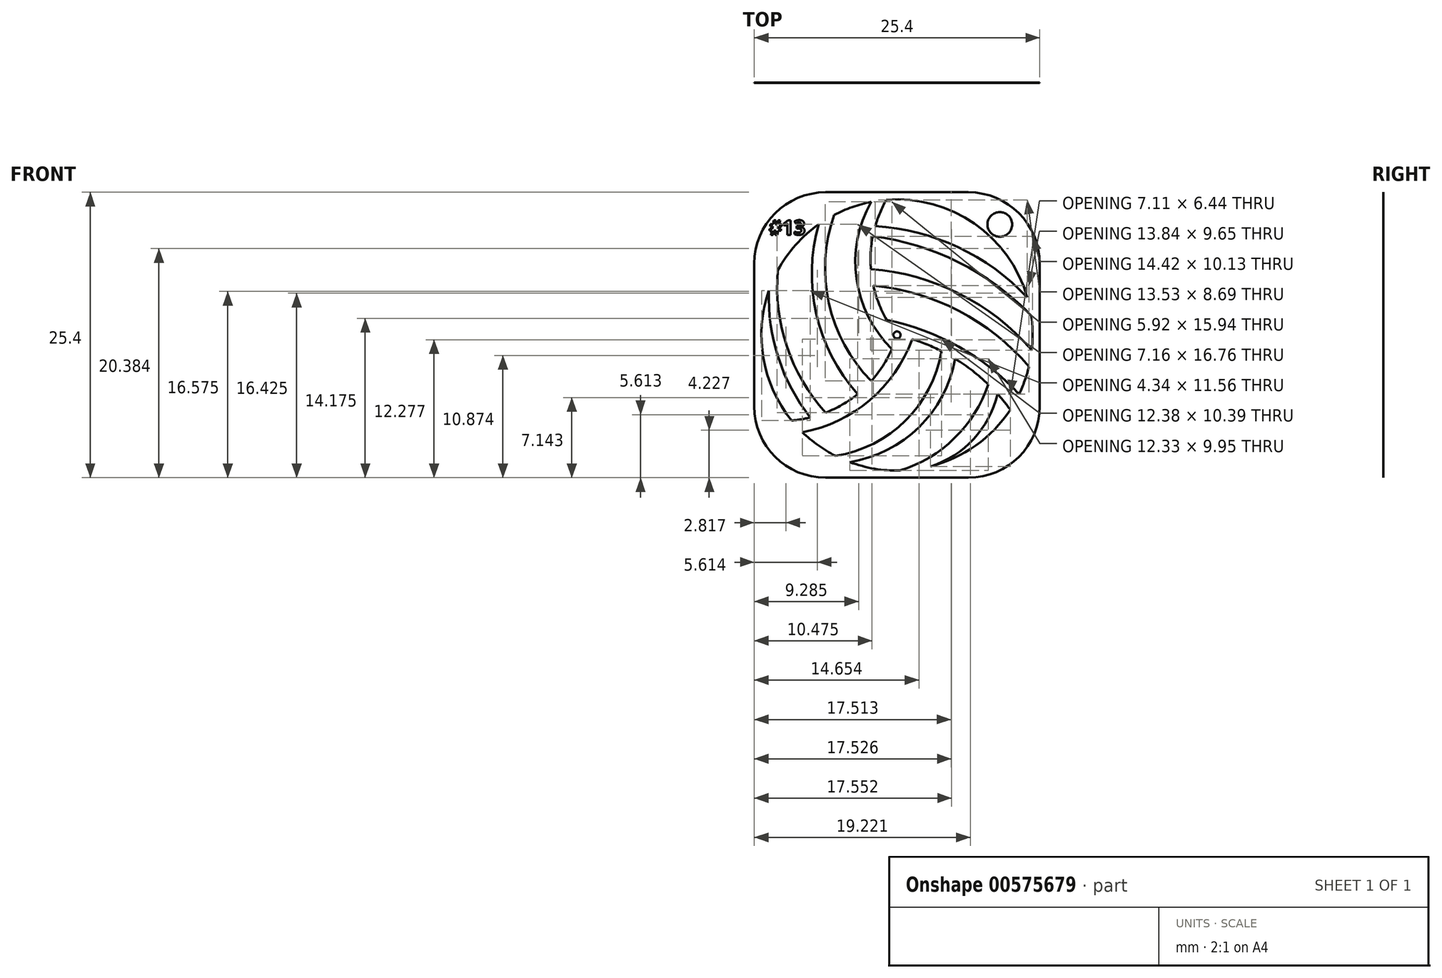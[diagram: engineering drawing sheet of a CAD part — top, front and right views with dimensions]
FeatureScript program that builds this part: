
annotation { "Feature Type Name" : "Feature", "Feature Type Description" : "" }
export const myFeature = defineFeature(function(context is Context, id is Id, definition is map)
    precondition{}
    {
        {
            var Q0;
            Q0=qCreatedBy(makeId("Front.planeOp"),FACE);
            var sketch = newSketch(context, id + "F0", { "sketchPlane" : qUnion([Q0])});
            skLineSegment(sketch, "E0", {"start": v(0, 6.35) * mm, "end": v(0, 19.05) * mm});
            skLineSegment(sketch, "E1", {"start": v(6.35, 0) * mm, "end": v(19.05, 0) * mm});
            skLineSegment(sketch, "E2", {"start": v(25.4, 6.35) * mm, "end": v(25.4, 19.05) * mm});
            skLineSegment(sketch, "E3", {"start": v(19.05, 25.4) * mm, "end": v(6.35, 25.4) * mm});
            skCircle(sketch, "E4", {"center": v(12.7, 12.7) * mm, "radius": 12.07 * mm});
            skPoint(sketch, "E5.visualSharp", {"position": v(0, 25.4) * mm});
            skArc(sketch, "E5.filletArc", {"start": v(6.35, 25.4) * mm, "mid": v(1.86, 23.54) * mm, "end": v(0, 19.05) * mm});
            skPoint(sketch, "E6.visualSharp", {"position": v(0, 0) * mm});
            skArc(sketch, "E6.filletArc", {"start": v(0, 6.35) * mm, "mid": v(1.86, 1.86) * mm, "end": v(6.35, 0) * mm});
            skPoint(sketch, "E7.visualSharp", {"position": v(25.4, 0) * mm});
            skArc(sketch, "E7.filletArc", {"start": v(19.05, 0) * mm, "mid": v(23.54, 1.86) * mm, "end": v(25.4, 6.35) * mm});
            skPoint(sketch, "E8.visualSharp", {"position": v(25.4, 25.4) * mm});
            skArc(sketch, "E8.filletArc", {"start": v(25.4, 19.05) * mm, "mid": v(23.54, 23.54) * mm, "end": v(19.05, 25.4) * mm});
            skPoint(sketch, "E9.centerSnap0", {"position": v(23.54, 23.54) * mm});
            skCircle(sketch, "E10", {"center": v(21.84, 22.54) * mm, "radius": 1.1 * mm});
            skPoint(sketch, "E9.center.orphan", {"position": v(21.97, 23.54) * mm});
            skArc(sketch, "E11", {"start": v(11.75, 24.73) * mm, "mid": v(10.37, 18.57) * mm, "end": v(12.7, 12.7) * mm});
            skArc(sketch, "E12", {"start": v(22.78, 6.06) * mm, "mid": v(18.34, 10.3) * mm, "end": v(12.7, 12.7) * mm});
            skArc(sketch, "E13", {"start": v(3.33, 5.1) * mm, "mid": v(9.2, 7.45) * mm, "end": v(12.7, 12.7) * mm});
            skLineSegment(sketch, "E14", {"start": v(15.68, 24.4) * mm, "end": v(15.68, 24.4) * mm});
            skPoint(sketch, "E15.start.orphan", {"position": v(19.05, 22.96) * mm});
            skArc(sketch, "E16", {"start": v(7.22, 1.95) * mm, "mid": v(13.45, 5.08) * mm, "end": v(16.67, 11.26) * mm});
            skArc(sketch, "E17", {"start": v(12.96, 0.64) * mm, "mid": v(17.81, 3.52) * mm, "end": v(20.82, 8.3) * mm});
            skArc(sketch, "E18", {"start": v(24.43, 9.9) * mm, "mid": v(18.2, 14.84) * mm, "end": v(10.6, 17.1) * mm});
            skArc(sketch, "E19", {"start": v(24.64, 14.44) * mm, "mid": v(18.2, 19.17) * mm, "end": v(10.54, 21.5) * mm});
            skArc(sketch, "E20", {"start": v(7.1, 23.4) * mm, "mid": v(6.64, 15.53) * mm, "end": v(10.4, 8.6) * mm});
            skArc(sketch, "E21", {"start": v(2.1, 18.46) * mm, "mid": v(2.9, 11.68) * mm, "end": v(6.35, 5.8) * mm});
            skArc(sketch, "E22", {"start": v(10.4, 24.54) * mm, "mid": v(9.1, 17.69) * mm, "end": v(12.25, 11.46) * mm});
            skArc(sketch, "E23", {"start": v(5.74, 22.56) * mm, "mid": v(5.52, 14.56) * mm, "end": v(9.2, 7.45) * mm});
            skArc(sketch, "E24", {"start": v(1.3, 16.65) * mm, "mid": v(2.14, 10.68) * mm, "end": v(4.99, 5.36) * mm});
            skArc(sketch, "E25", {"start": v(23.56, 7.45) * mm, "mid": v(18.19, 11.67) * mm, "end": v(11.78, 14.04) * mm});
            skArc(sketch, "E26", {"start": v(24.7, 11.36) * mm, "mid": v(18.24, 16.38) * mm, "end": v(10.37, 18.57) * mm});
            skArc(sketch, "E27", {"start": v(4.28, 4.05) * mm, "mid": v(10.27, 6.9) * mm, "end": v(14.04, 12.34) * mm});
            skArc(sketch, "E28", {"start": v(8.49, 1.4) * mm, "mid": v(14.65, 4.5) * mm, "end": v(17.87, 10.59) * mm});
            skArc(sketch, "E29", {"start": v(15.67, 1) * mm, "mid": v(19.5, 3.44) * mm, "end": v(21.65, 7.45) * mm});
            skPoint(sketch, "E30.start.orphan", {"position": v(24.3, 16.04) * mm});
            skArc(sketch, "E31", {"start": v(24.3, 16.04) * mm, "mid": v(18.13, 20.5) * mm, "end": v(10.76, 22.38) * mm});
            skCircle(sketch, "E32", {"center": v(12.7, 12.7) * mm, "radius": 0.32 * mm});
            skText(sketch, "E33", { "text": "#13", "fontName": "OpenSans-Bold.ttf"});
            skLineSegment(sketch, "E34", {"start": v(0.36, 21.14) * mm, "end": v(0.36, 5.6) * mm});
            skLineSegment(sketch, "E35", {"start": v(0.36, 17.45) * mm, "end": v(0, 17.45) * mm});
            const initialGuessF0  = {"E33": [0.00131, 0.02162, 1, 0, 0.0013], "E33": [0.00131, 0.02162, 1, 0, 0.0013]};
            skSetInitialGuess(sketch, initialGuessF0);
            skSolve(sketch);
        }
        {
            var Q0;
            Q0 = qSketchRegion(id + "F0", true);
            extrude(context, id + "F1", {"entities" : qUnion([Q0]), "depth" : 1 / 203.2 * mm, "offsetDistance" : 25.4 * mm});
        }
        {
            var Q0;
            Q0 = qSketchRegion(id + "F0", true);
            var Q1;
            {var subQ0=sQuery(id+"F0.wireOp",EDGE,"E20");Q1=makeQuery(id+"F0.imprint","IMPRINT",FACE,{"disambiguationData":[TD([[makeQuery(id+"F0.imprint","IMPRINT",EDGE,{"derivedFrom":subQ0}),-1.0]])]});}
            var Q2;
            {var subQ0=sQuery(id+"F0.wireOp",EDGE,"E21");Q2=makeQuery(id+"F0.imprint","IMPRINT",FACE,{"disambiguationData":[TD([[makeQuery(id+"F0.imprint","IMPRINT",EDGE,{"derivedFrom":subQ0}),-1.0]])]});}
            var Q3;
            {var subQ3=sQuery(id+"F0.wireOp",EDGE,"E22");Q3=makeQuery(id+"F0.imprint","IMPRINT",FACE,{"disambiguationData":[TD([[makeQuery(id+"F0.imprint","IMPRINT",EDGE,{"derivedFrom":subQ3}),1.0]])]});}
            var Q4;
            {var subQ5=sQuery(id+"F0.wireOp",EDGE,"E25");Q4=makeQuery(id+"F0.imprint","IMPRINT",FACE,{"disambiguationData":[TD([[makeQuery(id+"F0.imprint","IMPRINT",EDGE,{"derivedFrom":subQ5}),1.0]])]});}
            var Q5;
            {var subQ7=sQuery(id+"F0.wireOp",EDGE,"E27");Q5=makeQuery(id+"F0.imprint","IMPRINT",FACE,{"disambiguationData":[TD([[makeQuery(id+"F0.imprint","IMPRINT",EDGE,{"derivedFrom":subQ7}),1.0]])]});}
            var Q6;
            {var subQ0=sQuery(id+"F0.wireOp",EDGE,"E18");Q6=makeQuery(id+"F0.imprint","IMPRINT",FACE,{"disambiguationData":[TD([[makeQuery(id+"F0.imprint","IMPRINT",EDGE,{"derivedFrom":subQ0}),-1.0]])]});}
            var Q7;
            {var subQ0=sQuery(id+"F0.wireOp",EDGE,"E19");Q7=makeQuery(id+"F0.imprint","IMPRINT",FACE,{"disambiguationData":[TD([[makeQuery(id+"F0.imprint","IMPRINT",EDGE,{"derivedFrom":subQ0}),-1.0]])]});}
            var Q8;
            {var subQ0=sQuery(id+"F0.wireOp",EDGE,"E16");Q8=makeQuery(id+"F0.imprint","IMPRINT",FACE,{"disambiguationData":[TD([[makeQuery(id+"F0.imprint","IMPRINT",EDGE,{"derivedFrom":subQ0}),-1.0]])]});}
            var Q9;
            {var subQ0=sQuery(id+"F0.wireOp",EDGE,"E17");Q9=makeQuery(id+"F0.imprint","IMPRINT",FACE,{"disambiguationData":[TD([[makeQuery(id+"F0.imprint","IMPRINT",EDGE,{"derivedFrom":subQ0}),-1.0]])]});}
            extrude(context, id + "F2", {"entities" : qUnion([Q0, Q1, Q2, Q3, Q4, Q5, Q6, Q7, Q8, Q9]), "operationType" : NewBodyOperationType.ADD, "depth" : 1 / 203.2 * mm, "offsetDistance" : 25.4 * mm});
        }
        {
            var Q0;
            Q0=makeQuery(id+"F1.opExtrude","SWEPT_FACE",FACE,{"disambiguationData":[OSD([sQuery(id+"F0.wireOp",EDGE,"E0")])]});
            var sketch = newSketch(context, id + "F3", { "sketchPlane" : qUnion([Q0])});
            skText(sketch, "E36", { "text": "W", "fontName": "OpenSans-Bold.ttf"});
            skText(sketch, "E37", { "text": "H", "fontName": "OpenSans-Bold.ttf"});
            skText(sketch, "E38", { "text": "I", "fontName": "OpenSans-Bold.ttf"});
            skText(sketch, "E39", { "text": "T", "fontName": "OpenSans-Bold.ttf"});
            skText(sketch, "E40", { "text": "N", "fontName": "OpenSans-Bold.ttf"});
            skText(sketch, "E41", { "text": "A", "fontName": "OpenSans-Bold.ttf"});
            skText(sketch, "E42", { "text": "L", "fontName": "OpenSans-Bold.ttf"});
            skText(sketch, "E43", { "text": "L", "fontName": "OpenSans-Bold.ttf"});
            const initialGuessF3  = {"E36": [0.0007, 0.0175, 1, 0, 0.00141], "E37": [0.00101, 0.01592, 1, 0, 0.00143], "E38": [0.00143, 0.01432, 1, 0, 0.00141], "E39": [0.00118, 0.01278, 1, 0, 0.00135], "E40": [0.00104, 0.01111, 1, 0, 0.00142], "E41": [0.00107, 0.00954, 1, 0, 0.00145], "E42": [0.00124, 0.00802, 1, 0, 0.00143], "E43": [0.00124, 0.0065, 1, 0, 0.0014]};
            skSetInitialGuess(sketch, initialGuessF3);
            skSolve(sketch);
        }
        {
            var Q0;
            Q0 = qSketchRegion(id + "F3", true);
            extrude(context, id + "F4", {"entities" : qUnion([Q0]), "operationType" : NewBodyOperationType.REMOVE, "oppositeDirection" : true, "depth" : 0.36 * mm, "offsetDistance" : 25.4 * mm});
        }
        {
            var Q0;
            Q0=makeQuery(id+"F1.opExtrude","SWEPT_FACE",FACE,{"disambiguationData":[OSD([sQuery(id+"F0.wireOp",EDGE,"E2")])]});
            var sketch = newSketch(context, id + "F5", { "sketchPlane" : qUnion([Q0])});
            skText(sketch, "E44", { "text": "F", "fontName": "OpenSans-Bold.ttf"});
            skText(sketch, "E45", { "text": "A", "fontName": "OpenSans-Bold.ttf"});
            skText(sketch, "E46", { "text": "L", "fontName": "OpenSans-Bold.ttf"});
            skText(sketch, "E47", { "text": "C", "fontName": "OpenSans-Bold.ttf"});
            skText(sketch, "E48", { "text": "O", "fontName": "OpenSans-Bold.ttf"});
            skText(sketch, "E49", { "text": "N", "fontName": "OpenSans-Bold.ttf"});
            skText(sketch, "E50", { "text": "S", "fontName": "OpenSans-Bold.ttf"});
            skPoint(sketch, "E50.secondSnap0", {"position": v(-1.05, 9.23) * mm});
            const initialGuessF5  = {"E44": [-0.00245, 0.01734, 1, 0, 0.0015], "E45": [-0.00262, 0.0156, 1, 0, 0.0015], "E46": [-0.00245, 0.01377, 1, 0, 0.00164], "E47": [-0.00253, 0.01183, 1, 0, 0.00167], "E48": [-0.00257, 0.01018, 1, 0, 0.00141], "E49": [-0.00248, 0.00858, 1, 0, 0.00131], "E50": [-0.00217, 0.00688, 1, 0, 0.0014]};
            skSetInitialGuess(sketch, initialGuessF5);
            skSolve(sketch);
        }
        {
            var Q0;
            Q0 = qSketchRegion(id + "F5", true);
            extrude(context, id + "F6", {"entities" : qUnion([Q0]), "operationType" : NewBodyOperationType.REMOVE, "oppositeDirection" : true, "depth" : 0.36 * mm, "offsetDistance" : 25.4 * mm});
        }
    });
